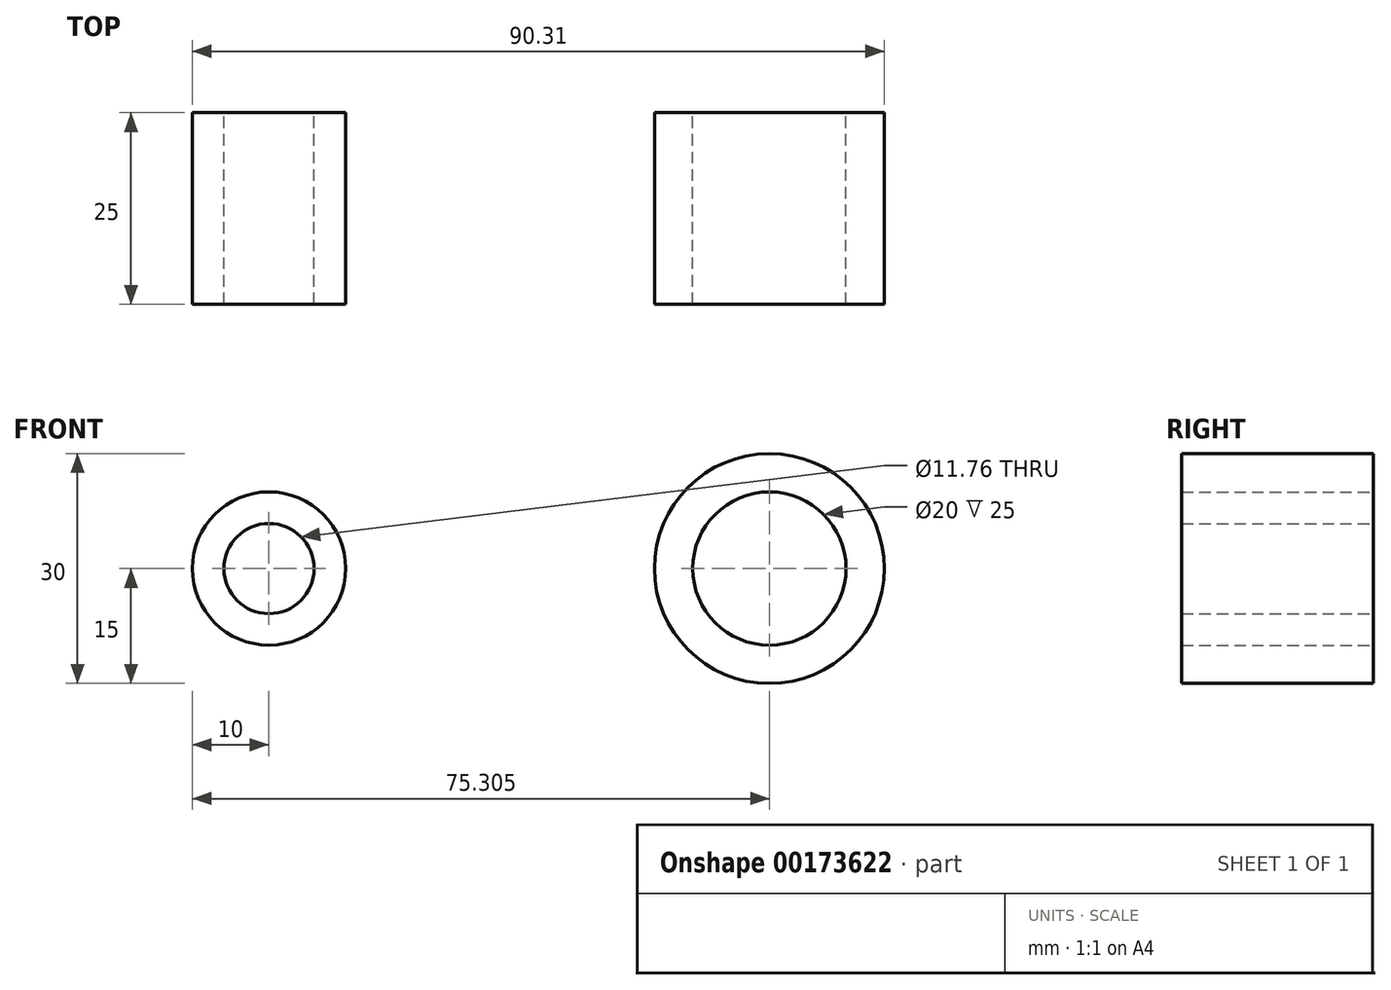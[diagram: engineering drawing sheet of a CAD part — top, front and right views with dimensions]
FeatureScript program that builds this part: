
annotation { "Feature Type Name" : "Feature", "Feature Type Description" : "" }
export const myFeature = defineFeature(function(context is Context, id is Id, definition is map)
    precondition{}
    {
        {
            var Q0;
            Q0=qCreatedBy(makeId("Front.planeOp"),FACE);
            var sketch = newSketch(context, id + "F0", { "sketchPlane" : qUnion([Q0])});
            skCircle(sketch, "E0", {"center": v(-29.55, 0) * mm, "radius": 10 * mm});
            skCircle(sketch, "E1", {"center": v(35.76, 0) * mm, "radius": 15 * mm});
            skCircle(sketch, "E2", {"center": v(-29.55, 0) * mm, "radius": 5.88 * mm});
            skCircle(sketch, "E3", {"center": v(35.76, 0) * mm, "radius": 10 * mm});
            skSolve(sketch);
        }
        {
            var Q0;
            Q0 = qSketchRegion(id + "F0", true);
            extrude(context, id + "F1", {"entities" : qUnion([Q0]), "depth" : 25 * mm});
        }
    });
